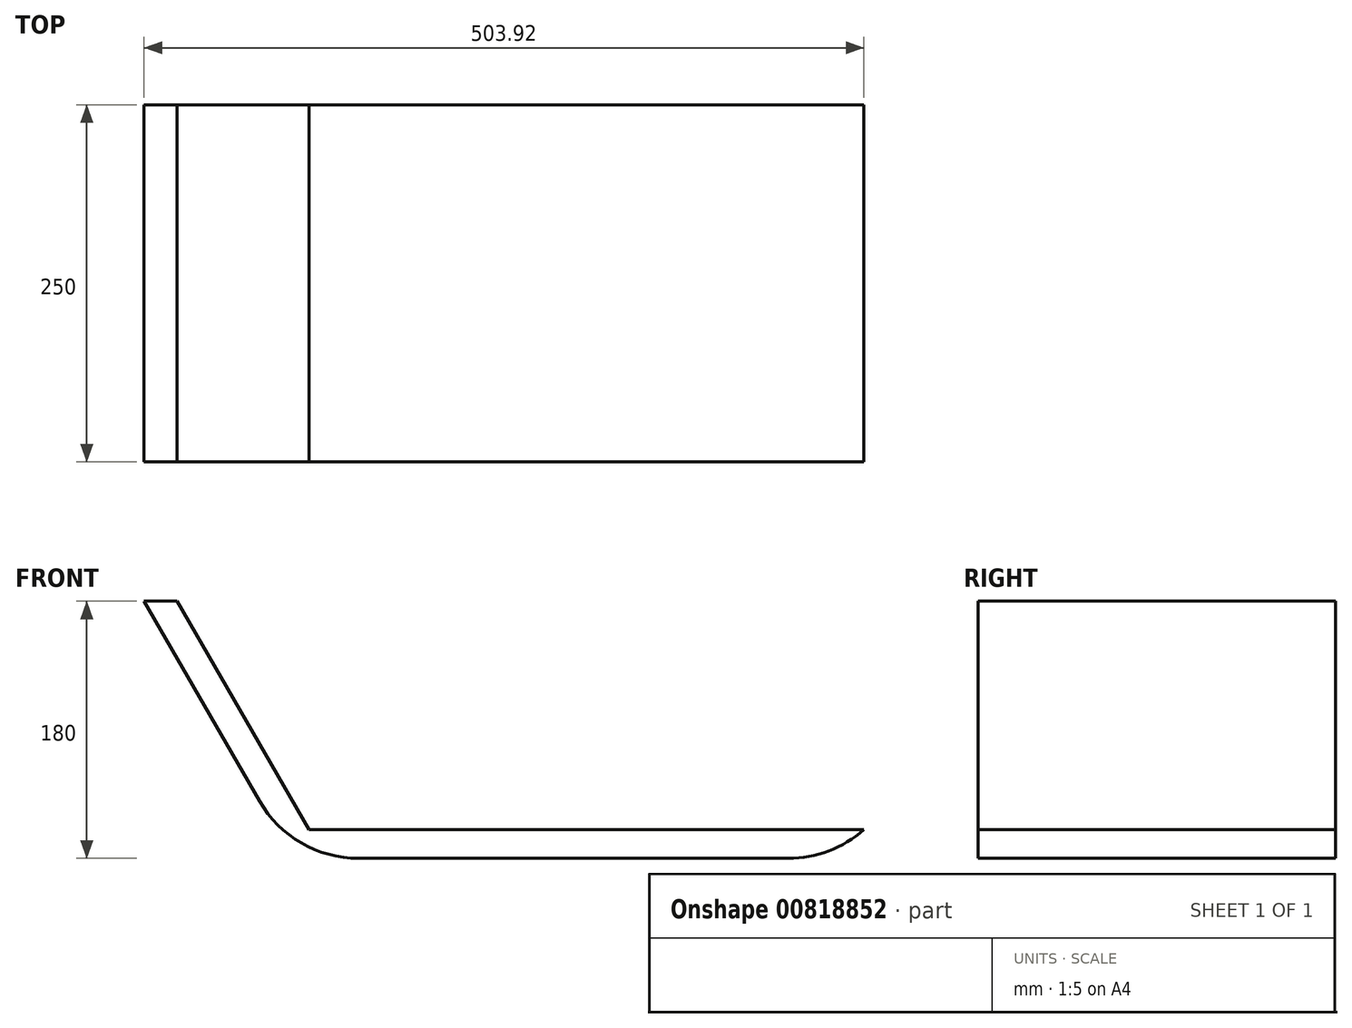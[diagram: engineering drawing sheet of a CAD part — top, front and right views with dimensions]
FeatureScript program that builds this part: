
annotation { "Feature Type Name" : "Feature", "Feature Type Description" : "" }
export const myFeature = defineFeature(function(context is Context, id is Id, definition is map)
    precondition{}
    {
        {
            var Q0;
            Q0=qCreatedBy(makeId("Top.planeOp"),FACE);
            var sketch = newSketch(context, id + "F0", { "sketchPlane" : qUnion([Q0])});
            skLineSegment(sketch, "E0.bottom", {"start": v(200, 125) * mm, "end": v(-200, 125) * mm});
            skLineSegment(sketch, "E0.top", {"start": v(200, -125) * mm, "end": v(-200, -125) * mm});
            skLineSegment(sketch, "E0.left", {"start": v(200, 125) * mm, "end": v(200, -125) * mm});
            skLineSegment(sketch, "E0.right", {"start": v(-200, 125) * mm, "end": v(-200, -125) * mm});
            skPoint(sketch, "E0.middle", {"position": v(0, 0) * mm});
            skSolve(sketch);
        }
        {
            var Q0;
            Q0 = qSketchRegion(id + "F0", true);
            extrude(context, id + "F1", {"entities" : qUnion([Q0]), "depth" : 20 * mm, "offsetDistance" : 25 * mm});
        }
        {
            var Q0;
            Q0=makeQuery(id+"F1.opExtrude","SWEPT_FACE",FACE,{"disambiguationData":[OSD([sQuery(id+"F0.wireOp",EDGE,"E0.top")])]});
            var sketch = newSketch(context, id + "F2", { "sketchPlane" : qUnion([Q0])});
            skLineSegment(sketch, "E1", {"start": v(-200, 0) * mm, "end": v(-303.92, 180) * mm});
            skLineSegment(sketch, "E2", {"start": v(-303.92, 180) * mm, "end": v(-280.83, 180) * mm});
            skLineSegment(sketch, "E3", {"start": v(-280.83, 180) * mm, "end": v(-188.45, 20) * mm});
            skLineSegment(sketch, "E4", {"start": v(-188.45, 20) * mm, "end": v(-200, 0) * mm});
            skSolve(sketch);
        }
        {
            var Q0;
            Q0 = qSketchRegion(id + "F2", true);
            var Q1;
            Q1=makeQuery(id+"F1.opExtrude","SWEPT_FACE",FACE,{"disambiguationData":[OSD([sQuery(id+"F0.wireOp",EDGE,"E0.bottom")])]});
            extrude(context, id + "F3", {"entities" : qUnion([Q0]), "operationType" : NewBodyOperationType.ADD, "endBound" : BoundingType.UP_TO_SURFACE, "oppositeDirection" : true, "depth" : 25 * mm, "endBoundEntityFace" : qUnion([Q1]), "offsetDistance" : 25 * mm});
        }
        {
            var Q0;
            Q0=makeQuery(id+"F3.opExtrude","SWEPT_EDGE",EDGE,{"disambiguationData":[OSD([sQuery(id+"F0.wireOp",EDGE,"E0.top"),sQuery(id+"F2.wireOp",EDGE,"E3"),sQuery(id+"F2.wireOp",EDGE,"E4")])]});
            var Q1;
            Q1=makeQuery(id+"F0NzBSYyiWk903m_1.1.F3.opExtrude","SWEPT_EDGE",EDGE,{"disambiguationData":[OSD([sQuery(id+"F0.wireOp",EDGE,"E0.top"),sQuery(id+"F2.wireOp",EDGE,"E3"),sQuery(id+"F2.wireOp",EDGE,"E4")])]});
            var Q2;
            {var subQ0=sQuery(id+"F0.wireOp",EDGE,"E0.right");Q2=makeQuery(id+"F3.boolean.opBoolean","MERGE",EDGE,{"derivedFrom":[makeQuery(id+"F1.opExtrude","CAP_EDGE",EDGE,{"disambiguationData":[OSD([subQ0])],"isStart":true}),makeQuery(id+"F3.opExtrude","SWEPT_EDGE",EDGE,{"disambiguationData":[OSD([sQuery(id+"F0.wireOp",EDGE,"E0.top"),subQ0,sQuery(id+"F2.wireOp",EDGE,"E1"),sQuery(id+"F2.wireOp",EDGE,"E4")])]})]});}
            var Q3;
            Q3=makeQuery(id+"F0NzBSYyiWk903m_1.1.F3.boolean.opBoolean","MERGE",EDGE,{"derivedFrom":[makeQuery(id+"F1.opExtrude","CAP_EDGE",EDGE,{"disambiguationData":[OSD([sQuery(id+"F0.wireOp",EDGE,"E0.left")])],"isStart":true}),makeQuery(id+"F0NzBSYyiWk903m_1.1.F3.opExtrude","SWEPT_EDGE",EDGE,{"disambiguationData":[OSD([sQuery(id+"F0.wireOp",EDGE,"E0.top"),sQuery(id+"F0.wireOp",EDGE,"E0.right"),sQuery(id+"F2.wireOp",EDGE,"E1"),sQuery(id+"F2.wireOp",EDGE,"E4")])]})]});
            fillet(context, id + "F4", {"entities" : qUnion([Q0, Q1, Q2, Q3]), "radius" : 80 * mm, "tangentPropagation" : true, "allowEdgeOverflow" : false});
        }
    });
